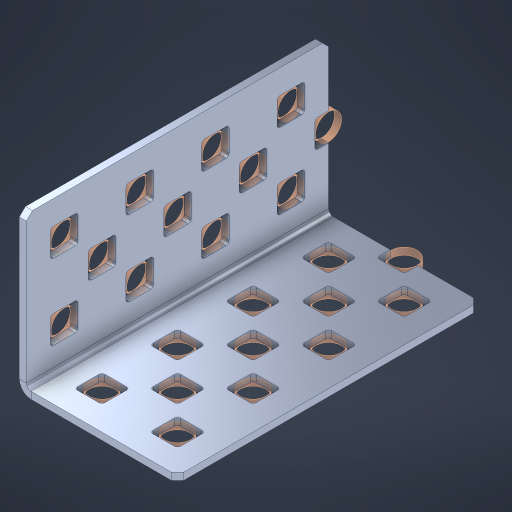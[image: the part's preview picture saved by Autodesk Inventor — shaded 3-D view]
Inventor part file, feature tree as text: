
AUTODESK INVENTOR PART (.ipt)
format: ipt  version: 2023 (Build 270158000, 158)  size: 601,600 bytes
history: native  units: in
note: dims shown in document units (in); Inventor stores cm internally (conversion verified against a paired STEP export)
features: other x30, extrude x22, sheet_metal_op x8, sketch x7, pattern_linear x2, mirror x1, chamfer x1
ambient origin geometry x8: Origin, YZ Plane, XZ Plane, XY Plane, X Axis, Y Axis, Z Axis, Center Point
bodies: Solid1 (feature_tree), Body (feature_tree)
feature tree (71):
  sheet_metal_op  "Flanges"
  sheet_metal_op  "Body Pattern"
  pattern_linear  "Center Pattern"  Spacing1=1.0in  [1 undecoded]
  other  "Arc Length"
  pattern_linear  "Notch Pattern"  Spacing1=0.1875in  [1 undecoded]
  other  "Diagonal Plane"
  mirror  "Everything Mirrored"
  chamfer  "End Chamfer"
  sketch  "Sketch1"  dims[d0=1.0in]
  other  "Plate1"
  sketch  "Sketch2"  dims[d1=2.0in]
  other  "Plate2"
  sheet_metal_op  "Bend1"
  sheet_metal_op  "Corner1"
  sketch  "Sketch8"  dims[d2=0.0469in]
  sketch  "Sketch9"  dims[d3=0.0469in]
  other  "Srf91"
  sheet_metal_op  "Body Pattern Sketch"
  other  "Srf92"
  sketch  "Sketch13"  dims[d4=0.0234in]
  sketch  "Sketch15"  dims[d5=0.0938in]
  sketch  "Sketch16"  dims[d6=0.0469in d7=1.0in d8=90.0deg d9=0.0312in d10=0.1875in d11=0.0469in d12=0.0469in d49=0.182in d50=0.02in d52=0.25in d53=0.0469in d54=0.0in d55=0.172in d56=1.0in d57=0.0in d60=1.5748in d62=0.5in d63=0.7874in d65=0.5in d85=0.1473in d86=0.1659in d89=0.0469in d90=0.0in d91=0.04in d92=0.0491in d95=2.5in d96=0.04in d97=0.25in d98=45.0deg d99=0.25in d106=0.182in d107=0.02in d108=0.5in d110=0.0469in d111=0.0in d112=0.172in d113=0.5in d114=0.0in d117=0.5in d123=0.25in d125=0.25in d126=0.0491in d127=0.1227in d128=0.08in d129=0.04in d130=2.5in]
  other  "Srf786"
  other  "Srf856"
  other  "Srf857"
  other  "Srf858"
  other  "Srf859"
  other  "Srf860"
  other  "Srf861"
  other  "Srf889"
  other  "Srf890"
  other  "Srf891"
  other  "Srf1275"
  other  "Srf1276"
  other  "Srf1278"
  other  "Srf1279"
  other  "Srf1280"
  other  "Srf1281"
  other  "Srf1282"
  other  "Srf1283"
  other  "Srf1277"
  other  "Srf1285"
  other  "Srf1286"
  other  "Srf1287"
  sheet_metal_op  "Body Stamp"
  sheet_metal_op  "Body Circle"
  other  "Center Stamp"
  other  "Center Circle"
  sheet_metal_op  "Notch"
  extrude  "ExtrusionSrf92"  Depth=0.0469in
  extrude  "ExtrusionSrf856"  Depth=0.0469in
  extrude  "ExtrusionSrf857"  Depth=0.182in
  extrude  "ExtrusionSrf858"  Depth=0.02in
  extrude  "ExtrusionSrf859"  Depth=0.25in
  extrude  "ExtrusionSrf860"  Depth=0.0469in
  extrude  "ExtrusionSrf861"  TaperAngle=0.0deg  [1 undecoded]
  extrude  "ExtrusionSrf889"  Depth=0.25in
  extrude  "ExtrusionSrf890"  Depth=1.0in TaperAngle=0.0deg
  extrude  "ExtrusionSrf891"  Depth=0.25in
  extrude  "ExtrusionSrf1275"  Depth=0.5in
  extrude  "ExtrusionSrf1276"  Depth=0.25in
  extrude  "ExtrusionSrf1277"  Depth=0.25in
  extrude  "ExtrusionSrf1278"  Depth=0.0469in
  extrude  "ExtrusionSrf1279"  Depth=0.25in TaperAngle=0.0deg
  extrude  "ExtrusionSrf1280"  Depth=0.25in
  extrude  "ExtrusionSrf1281"  Depth=0.25in TaperAngle=45.0deg
  extrude  "ExtrusionSrf1282"  Depth=0.25in
  extrude  "ExtrusionSrf1345"  Depth=0.182in
  extrude  "ExtrusionSrf1346"  Depth=0.02in
  extrude  "ExtrusionSrf1347"  Depth=0.5in
  extrude  "ExtrusionSrf1348"  Depth=0.0469in
note: 3 required parameter values undecoded (feature->parameter linkage not recoverable at this tier; creation-order binding heuristic only, values carry confidence <= 0.55)
